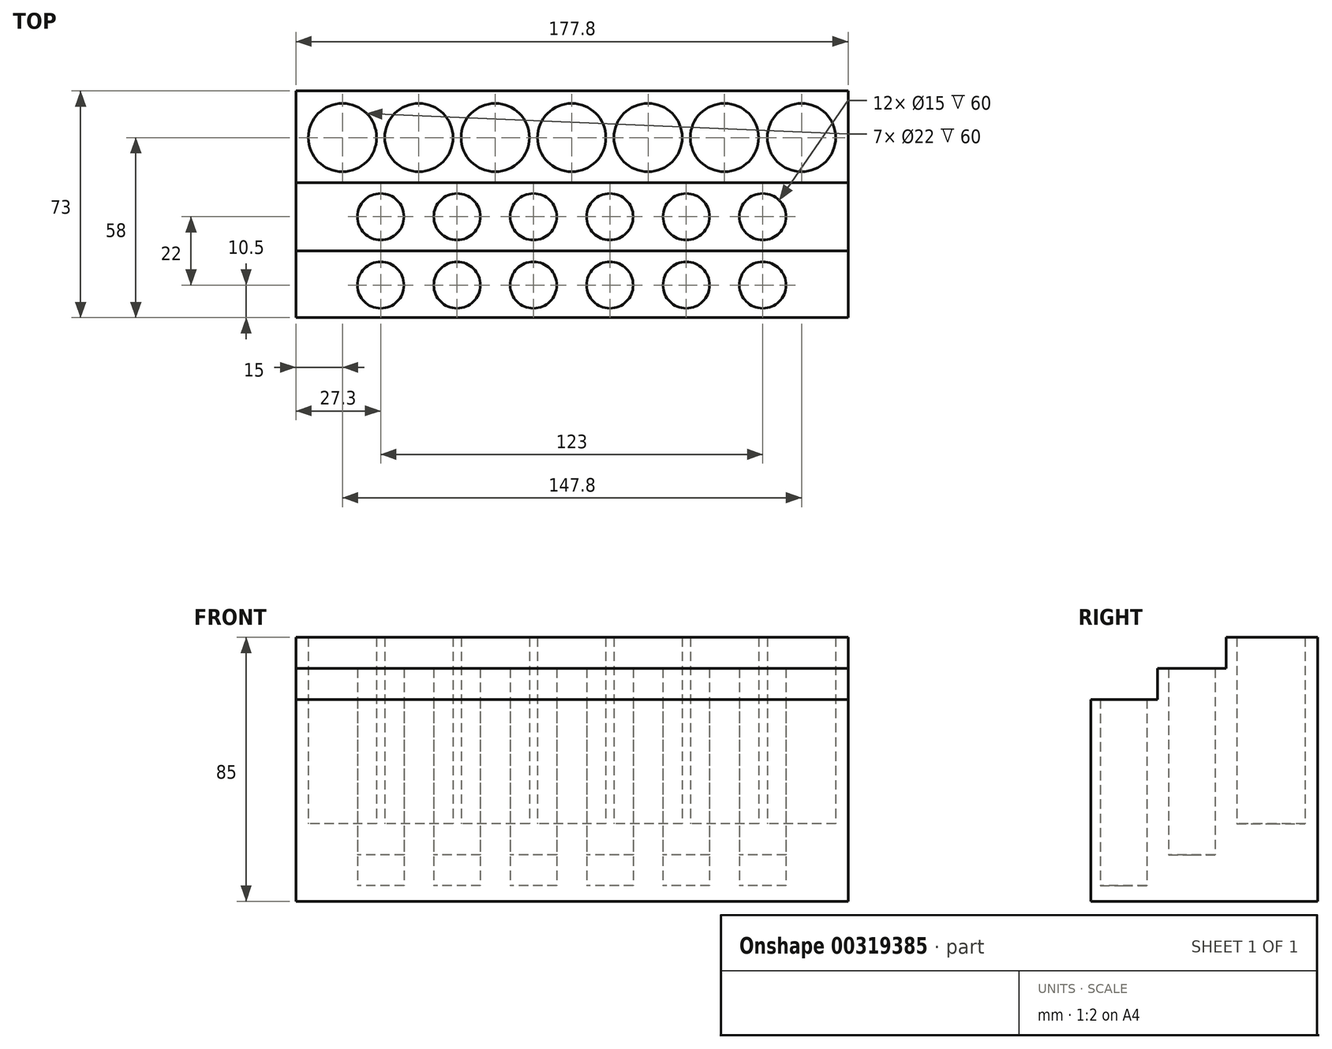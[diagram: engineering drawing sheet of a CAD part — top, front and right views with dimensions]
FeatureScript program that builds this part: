
annotation { "Feature Type Name" : "Feature", "Feature Type Description" : "" }
export const myFeature = defineFeature(function(context is Context, id is Id, definition is map)
    precondition{}
    {
        {
            var Q0;
            Q0=qCreatedBy(makeId("Top.planeOp"),FACE);
            var sketch = newSketch(context, id + "F0", { "sketchPlane" : qUnion([Q0])});
            skLineSegment(sketch, "E0.bottom", {"start": v(88.9, -36.5) * mm, "end": v(-88.9, -36.5) * mm});
            skLineSegment(sketch, "E0.top", {"start": v(88.9, 36.5) * mm, "end": v(-88.9, 36.5) * mm});
            skLineSegment(sketch, "E0.left", {"start": v(88.9, -36.5) * mm, "end": v(88.9, 36.5) * mm});
            skLineSegment(sketch, "E0.right", {"start": v(-88.9, -36.5) * mm, "end": v(-88.9, 36.5) * mm});
            skPoint(sketch, "E0.middle", {"position": v(0, 0) * mm});
            skLineSegment(sketch, "E1", {"start": v(-88.9, 21.5) * mm, "end": v(88.9, 21.5) * mm, "construction": true});
            skLineSegment(sketch, "E2", {"start": v(-73.9, 36.5) * mm, "end": v(-73.9, -36.5) * mm, "construction": true});
            skCircle(sketch, "E3", {"center": v(-73.9, 21.5) * mm, "radius": 11 * mm});
            skLineSegment(sketch, "E4", {"start": v(73.9, 36.5) * mm, "end": v(73.9, -36.5) * mm, "construction": true});
            skCircle(sketch, "E5", {"center": v(73.9, 21.5) * mm, "radius": 11 * mm});
            skLineSegment(sketch, "E6", {"start": v(-49.3, 36.5) * mm, "end": v(-49.3, -36.5) * mm, "construction": true});
            skCircle(sketch, "E7", {"center": v(-49.3, 21.5) * mm, "radius": 11 * mm});
            skCircle(sketch, "E8", {"center": v(-24.7, 21.5) * mm, "radius": 11 * mm});
            skCircle(sketch, "E9", {"center": v(-0.1, 21.5) * mm, "radius": 11 * mm});
            skCircle(sketch, "E10", {"center": v(24.5, 21.5) * mm, "radius": 11 * mm});
            skCircle(sketch, "E11", {"center": v(49.1, 21.5) * mm, "radius": 11 * mm});
            skLineSegment(sketch, "E12", {"start": v(-61.6, 36.5) * mm, "end": v(-61.6, -36.5) * mm, "construction": true});
            skCircle(sketch, "E13", {"center": v(-61.6, -4) * mm, "radius": 7.5 * mm});
            skLineSegment(sketch, "E14", {"start": v(-73.9, 10.5) * mm, "end": v(-49.3, 10.5) * mm, "construction": true});
            skCircle(sketch, "E15", {"center": v(-37, -4) * mm, "radius": 7.5 * mm});
            skCircle(sketch, "E16", {"center": v(-12.4, -4) * mm, "radius": 7.5 * mm});
            skCircle(sketch, "E17", {"center": v(12.2, -4) * mm, "radius": 7.5 * mm});
            skCircle(sketch, "E18", {"center": v(36.8, -4) * mm, "radius": 7.5 * mm});
            skCircle(sketch, "E19", {"center": v(61.4, -4) * mm, "radius": 7.5 * mm});
            skLineSegment(sketch, "E20", {"start": v(-61.6, -11.5) * mm, "end": v(-37, -11.5) * mm, "construction": true});
            skCircle(sketch, "E21", {"center": v(-61.6, -26) * mm, "radius": 7.5 * mm});
            skCircle(sketch, "E22", {"center": v(-37, -26) * mm, "radius": 7.5 * mm});
            skCircle(sketch, "E23", {"center": v(-12.4, -26) * mm, "radius": 7.5 * mm});
            skCircle(sketch, "E24", {"center": v(12.2, -26) * mm, "radius": 7.5 * mm});
            skCircle(sketch, "E25", {"center": v(36.8, -26) * mm, "radius": 7.5 * mm});
            skCircle(sketch, "E26", {"center": v(61.4, -26) * mm, "radius": 7.5 * mm});
            skLineSegment(sketch, "E27", {"start": v(-88.9, 7) * mm, "end": v(88.9, 7) * mm});
            skLineSegment(sketch, "E28", {"start": v(-88.9, -15) * mm, "end": v(88.9, -15) * mm});
            skSolve(sketch);
        }
        {
            var Q0;
            Q0=makeQuery(id+"F0.imprint","IMPRINT",FACE,{"disambiguationData":[TD([[makeQuery(id+"F0.imprint","IMPRINT",EDGE,{"derivedFrom":sQuery(id+"F0.wireOp",EDGE,"E18")}),1.0]])]});
            var Q1;
            Q1=makeQuery(id+"F0.imprint","IMPRINT",FACE,{"disambiguationData":[TD([[makeQuery(id+"F0.imprint","IMPRINT",EDGE,{"derivedFrom":sQuery(id+"F0.wireOp",EDGE,"E8")}),1.0]])]});
            var Q2;
            Q2=makeQuery(id+"F0.imprint","IMPRINT",FACE,{"disambiguationData":[TD([[makeQuery(id+"F0.imprint","IMPRINT",EDGE,{"derivedFrom":sQuery(id+"F0.wireOp",EDGE,"E7")}),1.0]])]});
            var Q3;
            Q3=makeQuery(id+"F0.imprint","IMPRINT",FACE,{"disambiguationData":[TD([[makeQuery(id+"F0.imprint","IMPRINT",EDGE,{"derivedFrom":sQuery(id+"F0.wireOp",EDGE,"E24")}),1.0]])]});
            var Q4;
            Q4=makeQuery(id+"F0.imprint","IMPRINT",FACE,{"disambiguationData":[TD([[makeQuery(id+"F0.imprint","IMPRINT",EDGE,{"derivedFrom":sQuery(id+"F0.wireOp",EDGE,"E16")}),1.0]])]});
            var Q5;
            {var subQ0=sQuery(id+"F0.wireOp",EDGE,"E0.top");Q5=makeQuery(id+"F0.imprint","IMPRINT",FACE,{"disambiguationData":[TD([[makeQuery(id+"F0.imprint","IMPRINT",EDGE,{"derivedFrom":subQ0}),1.0]])]});}
            var Q6;
            {var subQ1=sQuery(id+"F0.wireOp",EDGE,"E0.bottom");Q6=makeQuery(id+"F0.imprint","IMPRINT",FACE,{"disambiguationData":[TD([[makeQuery(id+"F0.imprint","IMPRINT",EDGE,{"derivedFrom":subQ1}),-1.0]])]});}
            var Q7;
            Q7=makeQuery(id+"F0.imprint","IMPRINT",FACE,{"disambiguationData":[TD([[makeQuery(id+"F0.imprint","IMPRINT",EDGE,{"derivedFrom":sQuery(id+"F0.wireOp",EDGE,"E23")}),1.0]])]});
            var Q8;
            Q8=makeQuery(id+"F0.imprint","IMPRINT",FACE,{"disambiguationData":[TD([[makeQuery(id+"F0.imprint","IMPRINT",EDGE,{"derivedFrom":sQuery(id+"F0.wireOp",EDGE,"E3")}),1.0]])]});
            var Q9;
            Q9=makeQuery(id+"F0.imprint","IMPRINT",FACE,{"disambiguationData":[TD([[makeQuery(id+"F0.imprint","IMPRINT",EDGE,{"derivedFrom":sQuery(id+"F0.wireOp",EDGE,"E10")}),1.0]])]});
            var Q10;
            Q10=makeQuery(id+"F0.imprint","IMPRINT",FACE,{"disambiguationData":[TD([[makeQuery(id+"F0.imprint","IMPRINT",EDGE,{"derivedFrom":sQuery(id+"F0.wireOp",EDGE,"E5")}),1.0]])]});
            var Q11;
            Q11=makeQuery(id+"F0.imprint","IMPRINT",FACE,{"disambiguationData":[TD([[makeQuery(id+"F0.imprint","IMPRINT",EDGE,{"derivedFrom":sQuery(id+"F0.wireOp",EDGE,"E11")}),1.0]])]});
            var Q12;
            Q12=makeQuery(id+"F0.imprint","IMPRINT",FACE,{"disambiguationData":[TD([[makeQuery(id+"F0.imprint","IMPRINT",EDGE,{"derivedFrom":sQuery(id+"F0.wireOp",EDGE,"E17")}),1.0]])]});
            var Q13;
            Q13=makeQuery(id+"F0.imprint","IMPRINT",FACE,{"disambiguationData":[TD([[makeQuery(id+"F0.imprint","IMPRINT",EDGE,{"derivedFrom":sQuery(id+"F0.wireOp",EDGE,"E19")}),1.0]])]});
            var Q14;
            Q14=makeQuery(id+"F0.imprint","IMPRINT",FACE,{"disambiguationData":[TD([[makeQuery(id+"F0.imprint","IMPRINT",EDGE,{"derivedFrom":sQuery(id+"F0.wireOp",EDGE,"E15")}),1.0]])]});
            var Q15;
            Q15=makeQuery(id+"F0.imprint","IMPRINT",FACE,{"disambiguationData":[TD([[makeQuery(id+"F0.imprint","IMPRINT",EDGE,{"derivedFrom":sQuery(id+"F0.wireOp",EDGE,"E9")}),1.0]])]});
            var Q16;
            Q16=makeQuery(id+"F0.imprint","IMPRINT",FACE,{"disambiguationData":[TD([[makeQuery(id+"F0.imprint","IMPRINT",EDGE,{"derivedFrom":sQuery(id+"F0.wireOp",EDGE,"E13")}),1.0]])]});
            var Q17;
            Q17=makeQuery(id+"F0.imprint","IMPRINT",FACE,{"disambiguationData":[TD([[makeQuery(id+"F0.imprint","IMPRINT",EDGE,{"derivedFrom":sQuery(id+"F0.wireOp",EDGE,"E22")}),1.0]])]});
            var Q18;
            Q18=makeQuery(id+"F0.imprint","IMPRINT",FACE,{"disambiguationData":[TD([[makeQuery(id+"F0.imprint","IMPRINT",EDGE,{"derivedFrom":sQuery(id+"F0.wireOp",EDGE,"E21")}),1.0]])]});
            var Q19;
            Q19=makeQuery(id+"F0.imprint","IMPRINT",FACE,{"disambiguationData":[TD([[makeQuery(id+"F0.imprint","IMPRINT",EDGE,{"derivedFrom":sQuery(id+"F0.wireOp",EDGE,"E26")}),1.0]])]});
            var Q20;
            Q20=makeQuery(id+"F0.imprint","IMPRINT",FACE,{"disambiguationData":[TD([[makeQuery(id+"F0.imprint","IMPRINT",EDGE,{"derivedFrom":sQuery(id+"F0.wireOp",EDGE,"E25")}),1.0]])]});
            var Q21;
            Q21=makeQuery(id+"F0.imprint","IMPRINT",FACE,{"disambiguationData":[TD([[makeQuery(id+"F0.imprint","IMPRINT",EDGE,{"derivedFrom":sQuery(id+"F0.wireOp",EDGE,"E13")}),-1.0]])]});
            extrude(context, id + "F1", {"entities" : qUnion([Q0, Q1, Q2, Q3, Q4, Q5, Q6, Q7, Q8, Q9, Q10, Q11, Q12, Q13, Q14, Q15, Q16, Q17, Q18, Q19, Q20, Q21]), "depth" : -5 * mm});
        }
        {
            var Q0;
            {var subQ1=sQuery(id+"F0.wireOp",EDGE,"E0.bottom");Q0=makeQuery(id+"F0.imprint","IMPRINT",FACE,{"disambiguationData":[TD([[makeQuery(id+"F0.imprint","IMPRINT",EDGE,{"derivedFrom":subQ1}),-1.0]])]});}
            extrude(context, id + "F2", {"entities" : qUnion([Q0]), "operationType" : NewBodyOperationType.ADD, "depth" : 60 * mm});
        }
        {
            var Q0;
            Q0=makeQuery(id+"F0.imprint","IMPRINT",FACE,{"disambiguationData":[TD([[makeQuery(id+"F0.imprint","IMPRINT",EDGE,{"derivedFrom":sQuery(id+"F0.wireOp",EDGE,"E13")}),-1.0]])]});
            var Q1;
            Q1=makeQuery(id+"F0.imprint","IMPRINT",FACE,{"disambiguationData":[TD([[makeQuery(id+"F0.imprint","IMPRINT",EDGE,{"derivedFrom":sQuery(id+"F0.wireOp",EDGE,"E13")}),1.0]])]});
            var Q2;
            Q2=makeQuery(id+"F0.imprint","IMPRINT",FACE,{"disambiguationData":[TD([[makeQuery(id+"F0.imprint","IMPRINT",EDGE,{"derivedFrom":sQuery(id+"F0.wireOp",EDGE,"E15")}),1.0]])]});
            var Q3;
            Q3=makeQuery(id+"F0.imprint","IMPRINT",FACE,{"disambiguationData":[TD([[makeQuery(id+"F0.imprint","IMPRINT",EDGE,{"derivedFrom":sQuery(id+"F0.wireOp",EDGE,"E16")}),1.0]])]});
            var Q4;
            Q4=makeQuery(id+"F0.imprint","IMPRINT",FACE,{"disambiguationData":[TD([[makeQuery(id+"F0.imprint","IMPRINT",EDGE,{"derivedFrom":sQuery(id+"F0.wireOp",EDGE,"E17")}),1.0]])]});
            var Q5;
            Q5=makeQuery(id+"F0.imprint","IMPRINT",FACE,{"disambiguationData":[TD([[makeQuery(id+"F0.imprint","IMPRINT",EDGE,{"derivedFrom":sQuery(id+"F0.wireOp",EDGE,"E18")}),1.0]])]});
            var Q6;
            Q6=makeQuery(id+"F0.imprint","IMPRINT",FACE,{"disambiguationData":[TD([[makeQuery(id+"F0.imprint","IMPRINT",EDGE,{"derivedFrom":sQuery(id+"F0.wireOp",EDGE,"E19")}),1.0]])]});
            extrude(context, id + "F3", {"entities" : qUnion([Q0, Q1, Q2, Q3, Q4, Q5, Q6]), "operationType" : NewBodyOperationType.ADD, "depth" : 70 * mm});
        }
        {
            var Q0;
            Q0=makeQuery(id+"F0.imprint","IMPRINT",FACE,{"disambiguationData":[TD([[makeQuery(id+"F0.imprint","IMPRINT",EDGE,{"derivedFrom":sQuery(id+"F0.wireOp",EDGE,"E13")}),1.0]])]});
            var Q1;
            Q1=makeQuery(id+"F0.imprint","IMPRINT",FACE,{"disambiguationData":[TD([[makeQuery(id+"F0.imprint","IMPRINT",EDGE,{"derivedFrom":sQuery(id+"F0.wireOp",EDGE,"E15")}),1.0]])]});
            var Q2;
            Q2=makeQuery(id+"F0.imprint","IMPRINT",FACE,{"disambiguationData":[TD([[makeQuery(id+"F0.imprint","IMPRINT",EDGE,{"derivedFrom":sQuery(id+"F0.wireOp",EDGE,"E16")}),1.0]])]});
            var Q3;
            Q3=makeQuery(id+"F0.imprint","IMPRINT",FACE,{"disambiguationData":[TD([[makeQuery(id+"F0.imprint","IMPRINT",EDGE,{"derivedFrom":sQuery(id+"F0.wireOp",EDGE,"E17")}),1.0]])]});
            var Q4;
            Q4=makeQuery(id+"F0.imprint","IMPRINT",FACE,{"disambiguationData":[TD([[makeQuery(id+"F0.imprint","IMPRINT",EDGE,{"derivedFrom":sQuery(id+"F0.wireOp",EDGE,"E18")}),1.0]])]});
            var Q5;
            Q5=makeQuery(id+"F0.imprint","IMPRINT",FACE,{"disambiguationData":[TD([[makeQuery(id+"F0.imprint","IMPRINT",EDGE,{"derivedFrom":sQuery(id+"F0.wireOp",EDGE,"E19")}),1.0]])]});
            var Q6;
            Q6=sQuery(id+"F0.wireOp",EDGE,"E13");
            var Q7;
            Q7=sQuery(id+"F0.wireOp",EDGE,"E15");
            var Q8;
            Q8=sQuery(id+"F0.wireOp",EDGE,"E16");
            var Q9;
            Q9=sQuery(id+"F0.wireOp",EDGE,"E17");
            var Q10;
            Q10=sQuery(id+"F0.wireOp",EDGE,"E18");
            var Q11;
            Q11=sQuery(id+"F0.wireOp",EDGE,"E19");
            extrude(context, id + "F4", {"entities" : qUnion([Q0, Q1, Q2, Q3, Q4, Q5]), "surfaceEntities" : qUnion([Q6, Q7, Q8, Q9, Q10, Q11]), "depth" : 70 * mm});
        }
        {
            var Q0;
            Q0=makeQuery(id+"F4.opExtrude","SWEPT_BODY",BODY,{"disambiguationData":[OSD([sQuery(id+"F0.wireOp",EDGE,"E13")])]});
            var Q1;
            Q1=makeQuery(id+"F4.opExtrude","SWEPT_BODY",BODY,{"disambiguationData":[OSD([sQuery(id+"F0.wireOp",EDGE,"E15")])]});
            var Q2;
            Q2=makeQuery(id+"F4.opExtrude","SWEPT_BODY",BODY,{"disambiguationData":[OSD([sQuery(id+"F0.wireOp",EDGE,"E16")])]});
            var Q3;
            Q3=makeQuery(id+"F4.opExtrude","SWEPT_BODY",BODY,{"disambiguationData":[OSD([sQuery(id+"F0.wireOp",EDGE,"E17")])]});
            var Q4;
            Q4=makeQuery(id+"F4.opExtrude","SWEPT_BODY",BODY,{"disambiguationData":[OSD([sQuery(id+"F0.wireOp",EDGE,"E18")])]});
            var Q5;
            Q5=makeQuery(id+"F4.opExtrude","SWEPT_BODY",BODY,{"disambiguationData":[OSD([sQuery(id+"F0.wireOp",EDGE,"E19")])]});
            transform(context, id + "F5", {"entities" : qUnion([Q0, Q1, Q2, Q3, Q4, Q5]), "transformType" : TransformType.TRANSLATION_3D, "dx" : 0 * mm, "dy" : 0 * mm, "dz" : 10 * mm, "makeCopy" : false});
        }
        {
            var Q0;
            Q0=makeQuery(id+"F4.opExtrude","SWEPT_BODY",BODY,{"disambiguationData":[OSD([sQuery(id+"F0.wireOp",EDGE,"E13")])]});
            var Q1;
            Q1=makeQuery(id+"F4.opExtrude","SWEPT_BODY",BODY,{"disambiguationData":[OSD([sQuery(id+"F0.wireOp",EDGE,"E15")])]});
            var Q2;
            Q2=makeQuery(id+"F4.opExtrude","SWEPT_BODY",BODY,{"disambiguationData":[OSD([sQuery(id+"F0.wireOp",EDGE,"E16")])]});
            var Q3;
            Q3=makeQuery(id+"F4.opExtrude","SWEPT_BODY",BODY,{"disambiguationData":[OSD([sQuery(id+"F0.wireOp",EDGE,"E17")])]});
            var Q4;
            Q4=makeQuery(id+"F4.opExtrude","SWEPT_BODY",BODY,{"disambiguationData":[OSD([sQuery(id+"F0.wireOp",EDGE,"E18")])]});
            var Q5;
            Q5=makeQuery(id+"F4.opExtrude","SWEPT_BODY",BODY,{"disambiguationData":[OSD([sQuery(id+"F0.wireOp",EDGE,"E19")])]});
            var Q6;
            Q6=makeQuery(id+"F1.opExtrude","SWEPT_BODY",BODY,{"disambiguationData":[OSD([sQuery(id+"F0.wireOp",EDGE,"E0.bottom"),sQuery(id+"F0.wireOp",EDGE,"E0.top"),sQuery(id+"F0.wireOp",EDGE,"E0.left"),sQuery(id+"F0.wireOp",EDGE,"E0.right")])]});
            booleanBodies(context, id + "F6", {"operationType" : BooleanOperationType.SUBTRACTION, "tools" : qUnion([Q0, Q1, Q2, Q3, Q4, Q5]), "targets" : qUnion([Q6])});
        }
        {
            var Q0;
            {var subQ0=sQuery(id+"F0.wireOp",EDGE,"E0.top");Q0=makeQuery(id+"F0.imprint","IMPRINT",FACE,{"disambiguationData":[TD([[makeQuery(id+"F0.imprint","IMPRINT",EDGE,{"derivedFrom":subQ0}),1.0]])]});}
            var Q1;
            Q1=makeQuery(id+"F0.imprint","IMPRINT",FACE,{"disambiguationData":[TD([[makeQuery(id+"F0.imprint","IMPRINT",EDGE,{"derivedFrom":sQuery(id+"F0.wireOp",EDGE,"E3")}),1.0]])]});
            var Q2;
            Q2=makeQuery(id+"F0.imprint","IMPRINT",FACE,{"disambiguationData":[TD([[makeQuery(id+"F0.imprint","IMPRINT",EDGE,{"derivedFrom":sQuery(id+"F0.wireOp",EDGE,"E7")}),1.0]])]});
            var Q3;
            Q3=makeQuery(id+"F0.imprint","IMPRINT",FACE,{"disambiguationData":[TD([[makeQuery(id+"F0.imprint","IMPRINT",EDGE,{"derivedFrom":sQuery(id+"F0.wireOp",EDGE,"E8")}),1.0]])]});
            var Q4;
            Q4=makeQuery(id+"F0.imprint","IMPRINT",FACE,{"disambiguationData":[TD([[makeQuery(id+"F0.imprint","IMPRINT",EDGE,{"derivedFrom":sQuery(id+"F0.wireOp",EDGE,"E9")}),1.0]])]});
            var Q5;
            Q5=makeQuery(id+"F0.imprint","IMPRINT",FACE,{"disambiguationData":[TD([[makeQuery(id+"F0.imprint","IMPRINT",EDGE,{"derivedFrom":sQuery(id+"F0.wireOp",EDGE,"E10")}),1.0]])]});
            var Q6;
            Q6=makeQuery(id+"F0.imprint","IMPRINT",FACE,{"disambiguationData":[TD([[makeQuery(id+"F0.imprint","IMPRINT",EDGE,{"derivedFrom":sQuery(id+"F0.wireOp",EDGE,"E11")}),1.0]])]});
            var Q7;
            Q7=makeQuery(id+"F0.imprint","IMPRINT",FACE,{"disambiguationData":[TD([[makeQuery(id+"F0.imprint","IMPRINT",EDGE,{"derivedFrom":sQuery(id+"F0.wireOp",EDGE,"E5")}),1.0]])]});
            extrude(context, id + "F7", {"entities" : qUnion([Q0, Q1, Q2, Q3, Q4, Q5, Q6, Q7]), "operationType" : NewBodyOperationType.ADD, "depth" : 80 * mm});
        }
        {
            var Q0;
            Q0=makeQuery(id+"F0.imprint","IMPRINT",FACE,{"disambiguationData":[TD([[makeQuery(id+"F0.imprint","IMPRINT",EDGE,{"derivedFrom":sQuery(id+"F0.wireOp",EDGE,"E3")}),1.0]])]});
            var Q1;
            Q1=makeQuery(id+"F0.imprint","IMPRINT",FACE,{"disambiguationData":[TD([[makeQuery(id+"F0.imprint","IMPRINT",EDGE,{"derivedFrom":sQuery(id+"F0.wireOp",EDGE,"E7")}),1.0]])]});
            var Q2;
            Q2=makeQuery(id+"F0.imprint","IMPRINT",FACE,{"disambiguationData":[TD([[makeQuery(id+"F0.imprint","IMPRINT",EDGE,{"derivedFrom":sQuery(id+"F0.wireOp",EDGE,"E8")}),1.0]])]});
            var Q3;
            Q3=makeQuery(id+"F0.imprint","IMPRINT",FACE,{"disambiguationData":[TD([[makeQuery(id+"F0.imprint","IMPRINT",EDGE,{"derivedFrom":sQuery(id+"F0.wireOp",EDGE,"E9")}),1.0]])]});
            var Q4;
            Q4=makeQuery(id+"F0.imprint","IMPRINT",FACE,{"disambiguationData":[TD([[makeQuery(id+"F0.imprint","IMPRINT",EDGE,{"derivedFrom":sQuery(id+"F0.wireOp",EDGE,"E10")}),1.0]])]});
            var Q5;
            Q5=makeQuery(id+"F0.imprint","IMPRINT",FACE,{"disambiguationData":[TD([[makeQuery(id+"F0.imprint","IMPRINT",EDGE,{"derivedFrom":sQuery(id+"F0.wireOp",EDGE,"E11")}),1.0]])]});
            var Q6;
            Q6=makeQuery(id+"F0.imprint","IMPRINT",FACE,{"disambiguationData":[TD([[makeQuery(id+"F0.imprint","IMPRINT",EDGE,{"derivedFrom":sQuery(id+"F0.wireOp",EDGE,"E5")}),1.0]])]});
            var Q7;
            Q7=sQuery(id+"F0.wireOp",EDGE,"E3");
            var Q8;
            Q8=sQuery(id+"F0.wireOp",EDGE,"E7");
            var Q9;
            Q9=sQuery(id+"F0.wireOp",EDGE,"E8");
            var Q10;
            Q10=sQuery(id+"F0.wireOp",EDGE,"E9");
            var Q11;
            Q11=sQuery(id+"F0.wireOp",EDGE,"E10");
            var Q12;
            Q12=sQuery(id+"F0.wireOp",EDGE,"E11");
            var Q13;
            Q13=sQuery(id+"F0.wireOp",EDGE,"E5");
            extrude(context, id + "F8", {"entities" : qUnion([Q0, Q1, Q2, Q3, Q4, Q5, Q6]), "surfaceEntities" : qUnion([Q7, Q8, Q9, Q10, Q11, Q12, Q13]), "depth" : 90 * mm});
        }
        {
            var Q0;
            Q0=makeQuery(id+"F8.opExtrude","SWEPT_BODY",BODY,{"disambiguationData":[OSD([sQuery(id+"F0.wireOp",EDGE,"E3")])]});
            var Q1;
            Q1=makeQuery(id+"F8.opExtrude","SWEPT_BODY",BODY,{"disambiguationData":[OSD([sQuery(id+"F0.wireOp",EDGE,"E5")])]});
            var Q2;
            Q2=makeQuery(id+"F8.opExtrude","SWEPT_BODY",BODY,{"disambiguationData":[OSD([sQuery(id+"F0.wireOp",EDGE,"E7")])]});
            var Q3;
            Q3=makeQuery(id+"F8.opExtrude","SWEPT_BODY",BODY,{"disambiguationData":[OSD([sQuery(id+"F0.wireOp",EDGE,"E8")])]});
            var Q4;
            Q4=makeQuery(id+"F8.opExtrude","SWEPT_BODY",BODY,{"disambiguationData":[OSD([sQuery(id+"F0.wireOp",EDGE,"E9")])]});
            var Q5;
            Q5=makeQuery(id+"F8.opExtrude","SWEPT_BODY",BODY,{"disambiguationData":[OSD([sQuery(id+"F0.wireOp",EDGE,"E10")])]});
            var Q6;
            Q6=makeQuery(id+"F8.opExtrude","SWEPT_BODY",BODY,{"disambiguationData":[OSD([sQuery(id+"F0.wireOp",EDGE,"E11")])]});
            transform(context, id + "F9", {"entities" : qUnion([Q0, Q1, Q2, Q3, Q4, Q5, Q6]), "transformType" : TransformType.TRANSLATION_3D, "dx" : 0 * mm, "dy" : 0 * mm, "dz" : 20 * mm, "makeCopy" : false});
        }
        {
            var Q0;
            Q0=makeQuery(id+"F8.opExtrude","SWEPT_BODY",BODY,{"disambiguationData":[OSD([sQuery(id+"F0.wireOp",EDGE,"E3")])]});
            var Q1;
            Q1=makeQuery(id+"F8.opExtrude","SWEPT_BODY",BODY,{"disambiguationData":[OSD([sQuery(id+"F0.wireOp",EDGE,"E5")])]});
            var Q2;
            Q2=makeQuery(id+"F8.opExtrude","SWEPT_BODY",BODY,{"disambiguationData":[OSD([sQuery(id+"F0.wireOp",EDGE,"E7")])]});
            var Q3;
            Q3=makeQuery(id+"F8.opExtrude","SWEPT_BODY",BODY,{"disambiguationData":[OSD([sQuery(id+"F0.wireOp",EDGE,"E8")])]});
            var Q4;
            Q4=makeQuery(id+"F8.opExtrude","SWEPT_BODY",BODY,{"disambiguationData":[OSD([sQuery(id+"F0.wireOp",EDGE,"E9")])]});
            var Q5;
            Q5=makeQuery(id+"F8.opExtrude","SWEPT_BODY",BODY,{"disambiguationData":[OSD([sQuery(id+"F0.wireOp",EDGE,"E10")])]});
            var Q6;
            Q6=makeQuery(id+"F8.opExtrude","SWEPT_BODY",BODY,{"disambiguationData":[OSD([sQuery(id+"F0.wireOp",EDGE,"E11")])]});
            var Q7;
            Q7=makeQuery(id+"F1.opExtrude","SWEPT_BODY",BODY,{"disambiguationData":[OSD([sQuery(id+"F0.wireOp",EDGE,"E0.bottom"),sQuery(id+"F0.wireOp",EDGE,"E0.top"),sQuery(id+"F0.wireOp",EDGE,"E0.left"),sQuery(id+"F0.wireOp",EDGE,"E0.right")])]});
            booleanBodies(context, id + "F10", {"operationType" : BooleanOperationType.SUBTRACTION, "tools" : qUnion([Q0, Q1, Q2, Q3, Q4, Q5, Q6]), "targets" : qUnion([Q7])});
        }
    });
